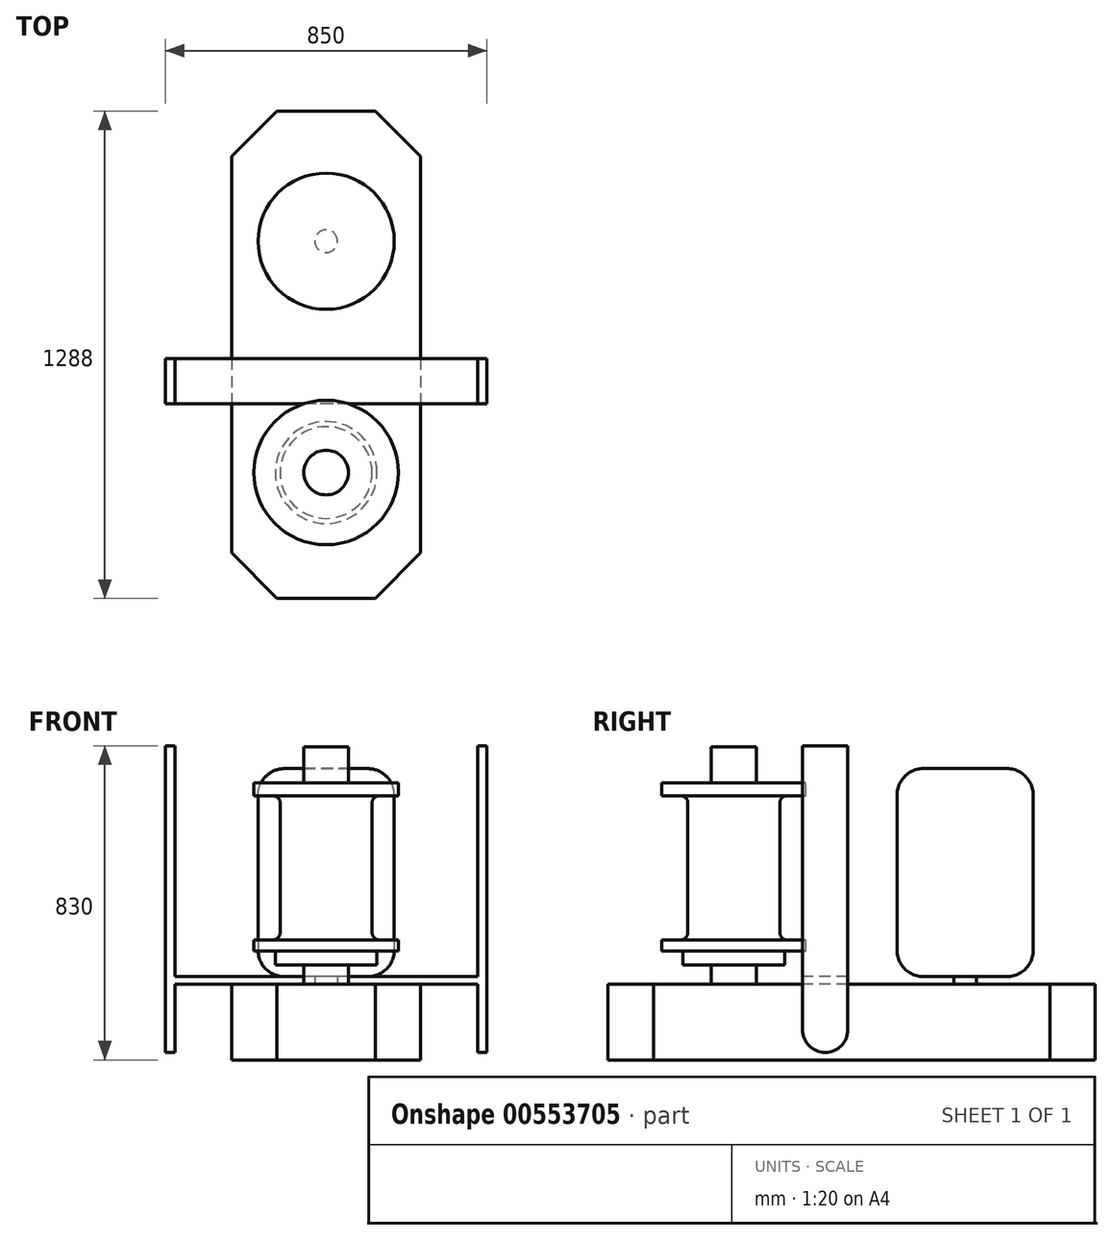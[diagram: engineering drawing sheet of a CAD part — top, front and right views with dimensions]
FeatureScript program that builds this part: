
annotation { "Feature Type Name" : "Feature", "Feature Type Description" : "" }
export const myFeature = defineFeature(function(context is Context, id is Id, definition is map)
    precondition{}
    {
        {
            var Q0;
            Q0=qCreatedBy(makeId("Top.planeOp"),FACE);
            var sketch = newSketch(context, id + "F0", { "sketchPlane" : qUnion([Q0])});
            skLineSegment(sketch, "E0.bottom", {"start": v(-130, 644) * mm, "end": v(130, 644) * mm});
            skLineSegment(sketch, "E0.top", {"start": v(-130, -644) * mm, "end": v(130, -644) * mm});
            skLineSegment(sketch, "E0.left", {"start": v(-250, 524) * mm, "end": v(-250, -524) * mm});
            skLineSegment(sketch, "E0.right", {"start": v(250, 524) * mm, "end": v(250, -524) * mm});
            skLineSegment(sketch, "E1", {"start": v(-130, 644) * mm, "end": v(-250, 524) * mm});
            skLineSegment(sketch, "E2", {"start": v(130, 644) * mm, "end": v(250, 524) * mm});
            skPoint(sketch, "E3.orphan", {"position": v(-250, 644) * mm});
            skPoint(sketch, "E4.orphan", {"position": v(250, 644) * mm});
            skLineSegment(sketch, "E5", {"start": v(-250, -524) * mm, "end": v(-130, -644) * mm});
            skPoint(sketch, "E6.orphan", {"position": v(-250, -644) * mm});
            skLineSegment(sketch, "E7", {"start": v(130, -644) * mm, "end": v(250, -524) * mm});
            skPoint(sketch, "E8.orphan", {"position": v(250, -644) * mm});
            skSolve(sketch);
        }
        {
            var Q0;
            Q0 = qSketchRegion(id + "F0", true);
            extrude(context, id + "F1", {"entities" : qUnion([Q0]), "depth" : 200 * mm, "offsetDistance" : 25 * mm});
        }
        {
            var Q0;
            Q0=makeQuery(id+"F1.opExtrude","CAP_FACE",FACE,{"disambiguationData":[OSD([sQuery(id+"F0.wireOp",EDGE,"E0.bottom"),sQuery(id+"F0.wireOp",EDGE,"E0.top"),sQuery(id+"F0.wireOp",EDGE,"E0.left"),sQuery(id+"F0.wireOp",EDGE,"E0.right"),sQuery(id+"F0.wireOp",EDGE,"E1"),sQuery(id+"F0.wireOp",EDGE,"E2"),sQuery(id+"F0.wireOp",EDGE,"E5"),sQuery(id+"F0.wireOp",EDGE,"E7")])],"isStart":false});
            var sketch = newSketch(context, id + "F2", { "sketchPlane" : qUnion([Q0])});
            skCircle(sketch, "E9", {"center": v(0, 300) * mm, "radius": 30 * mm});
            skSolve(sketch);
        }
        {
            var Q0;
            Q0=makeQuery(id+"F2.imprint","IMPRINT",FACE,{"disambiguationData":[TD([[makeQuery(id+"F2.imprint","IMPRINT",EDGE,{"derivedFrom":sQuery(id+"F2.wireOp",EDGE,"E9")}),1.0]])]});
            var Q1;
            Q1=sQuery(id+"F2.wireOp",EDGE,"E9");
            extrude(context, id + "F3", {"entities" : qUnion([Q0]), "surfaceEntities" : qUnion([Q1]), "depth" : 20 * mm, "offsetDistance" : 25 * mm});
        }
        {
            var Q0;
            Q0=makeQuery(id+"F3.opExtrude","CAP_FACE",FACE,{"disambiguationData":[OSD([sQuery(id+"F2.wireOp",EDGE,"E9")])],"isStart":false});
            var sketch = newSketch(context, id + "F4", { "sketchPlane" : qUnion([Q0])});
            skCircle(sketch, "E10", {"center": v(0, 300) * mm, "radius": 180 * mm});
            skSolve(sketch);
        }
        {
            var Q0;
            Q0=makeQuery(id+"F4.imprint","IMPRINT",FACE,{"disambiguationData":[TD([[makeQuery(id+"F4.imprint","IMPRINT",EDGE,{"derivedFrom":sQuery(id+"F4.wireOp",EDGE,"E10")}),1.0]])]});
            var Q1;
            Q1=makeQuery(id+"F4.imprint","IMPRINT",FACE,{"disambiguationData":[TD([[makeQuery(id+"F4.imprint","IMPRINT",EDGE,{"derivedFrom":makeQuery(id+"F3.opExtrude","CAP_EDGE",EDGE,{"disambiguationData":[OSD([sQuery(id+"F2.wireOp",EDGE,"E9")])],"isStart":false})}),1.0]])]});
            extrude(context, id + "F5", {"entities" : qUnion([Q0, Q1]), "operationType" : NewBodyOperationType.ADD, "depth" : 550 * mm, "offsetDistance" : 25 * mm});
        }
        {
            var Q0;
            Q0=makeQuery(id+"F5.opExtrude","CAP_EDGE",EDGE,{"disambiguationData":[OSD([sQuery(id+"F4.wireOp",EDGE,"E10")])],"isStart":false});
            var Q1;
            Q1=makeQuery(id+"F5.opExtrude","CAP_EDGE",EDGE,{"disambiguationData":[OSD([sQuery(id+"F4.wireOp",EDGE,"E10")])],"isStart":true});
            fillet(context, id + "F6", {"entities" : qUnion([Q0, Q1]), "radius" : 70 * mm, "tangentPropagation" : true, "allowEdgeOverflow" : false});
        }
        {
            var Q0;
            Q0=qCreatedBy(makeId("Right.planeOp"),FACE);
            var sketch = newSketch(context, id + "F7", { "sketchPlane" : qUnion([Q0])});
            skLineSegment(sketch, "E11", {"start": v(-311.44, 828) * mm, "end": v(-311.44, 180.1) * mm});
            skLineSegment(sketch, "E12", {"start": v(-311.44, 828) * mm, "end": v(-370.59, 828) * mm});
            skLineSegment(sketch, "E13", {"start": v(-370.59, 828) * mm, "end": v(-370.59, 732.1) * mm});
            skLineSegment(sketch, "E14", {"start": v(-370.59, 732.1) * mm, "end": v(-454.79, 732.1) * mm});
            skLineSegment(sketch, "E15", {"start": v(-454.79, 732.1) * mm, "end": v(-502.39, 732.1) * mm});
            skLineSegment(sketch, "E16", {"start": v(-502.39, 732.1) * mm, "end": v(-502.39, 698.5) * mm});
            skLineSegment(sketch, "E17", {"start": v(-502.39, 698.5) * mm, "end": v(-452.84, 698.5) * mm});
            skLineSegment(sketch, "E18", {"start": v(-432.84, 678.5) * mm, "end": v(-432.84, 337.2) * mm});
            skLineSegment(sketch, "E19", {"start": v(-452.84, 317.2) * mm, "end": v(-502.39, 317.2) * mm});
            skLineSegment(sketch, "E20", {"start": v(-502.39, 317.2) * mm, "end": v(-502.39, 287.86) * mm});
            skLineSegment(sketch, "E21", {"start": v(-502.39, 287.86) * mm, "end": v(-445.97, 287.86) * mm});
            skLineSegment(sketch, "E22", {"start": v(-445.97, 287.86) * mm, "end": v(-445.97, 250.88) * mm});
            skLineSegment(sketch, "E23", {"start": v(-445.97, 250.88) * mm, "end": v(-370.59, 250.88) * mm});
            skLineSegment(sketch, "E24", {"start": v(-370.59, 250.88) * mm, "end": v(-370.59, 175.63) * mm});
            skLineSegment(sketch, "E25", {"start": v(-370.59, 175.63) * mm, "end": v(-311.44, 180.1) * mm});
            skPoint(sketch, "E26.visualSharp", {"position": v(-432.84, 317.2) * mm});
            skArc(sketch, "E26.filletArc", {"start": v(-452.84, 317.2) * mm, "mid": v(-438.7, 323.05) * mm, "end": v(-432.84, 337.2) * mm});
            skPoint(sketch, "E27.visualSharp", {"position": v(-432.84, 698.5) * mm});
            skArc(sketch, "E27.filletArc", {"start": v(-432.84, 678.5) * mm, "mid": v(-438.7, 692.65) * mm, "end": v(-452.84, 698.5) * mm});
            skSolve(sketch);
        }
        {
            var Q0;
            Q0=makeQuery(id+"F7.imprint","IMPRINT",FACE,{"disambiguationData":[TD([[makeQuery(id+"F7.imprint","IMPRINT",EDGE,{"derivedFrom":sQuery(id+"F7.wireOp",EDGE,"E11")}),-1.0]])]});
            var Q1;
            Q1=sQuery(id+"F7.wireOp",EDGE,"E11");
            revolve(context, id + "F8", {"operationType" : NewBodyOperationType.ADD, "entities" : qUnion([Q0]), "axis" : qUnion([Q1]), "revolveType" : RevolveType.FULL});
        }
        {
            var Q0;
            Q0=makeQuery(id+"F1.opExtrude","CAP_FACE",FACE,{"disambiguationData":[OSD([sQuery(id+"F0.wireOp",EDGE,"E0.bottom"),sQuery(id+"F0.wireOp",EDGE,"E0.top"),sQuery(id+"F0.wireOp",EDGE,"E0.left"),sQuery(id+"F0.wireOp",EDGE,"E0.right"),sQuery(id+"F0.wireOp",EDGE,"E1"),sQuery(id+"F0.wireOp",EDGE,"E2"),sQuery(id+"F0.wireOp",EDGE,"E5"),sQuery(id+"F0.wireOp",EDGE,"E7")])],"isStart":false});
            var sketch = newSketch(context, id + "F9", { "sketchPlane" : qUnion([Q0])});
            skLineSegment(sketch, "E28.bottom", {"start": v(400, -10) * mm, "end": v(-400, -10) * mm});
            skLineSegment(sketch, "E28.top", {"start": v(400, -130) * mm, "end": v(-400, -130) * mm});
            skLineSegment(sketch, "E28.left", {"start": v(400, -10) * mm, "end": v(400, -130) * mm});
            skLineSegment(sketch, "E28.right", {"start": v(-400, -10) * mm, "end": v(-400, -130) * mm});
            skSolve(sketch);
        }
        {
            var Q0;
            {var subQ0=sQuery(id+"F9.wireOp",EDGE,"E28.left");Q0=makeQuery(id+"F9.imprint","IMPRINT",FACE,{"disambiguationData":[TD([[makeQuery(id+"F9.imprint","IMPRINT",EDGE,{"derivedFrom":subQ0}),-1.0]])]});}
            var Q1;
            {var subQ0=sQuery(id+"F9.wireOp",EDGE,"E28.bottom");var subQ1=makeQuery(id+"F1.opExtrude","CAP_EDGE",EDGE,{"disambiguationData":[OSD([sQuery(id+"F0.wireOp",EDGE,"E0.right")])],"isStart":false});var subQ2=makeQuery(id+"F9.imprint","INTERSECT",VERTEX,{"derivedFrom":[subQ1,subQ0]});Q1=makeQuery(id+"F9.imprint","IMPRINT",FACE,{"disambiguationData":[TD([[makeQuery(id+"F9.imprint","IMPRINT",EDGE,{"disambiguationData":[TD([[subQ2,-1.0]])],"derivedFrom":subQ0}),1.0]])]});}
            var Q2;
            {var subQ0=sQuery(id+"F9.wireOp",EDGE,"E28.right");Q2=makeQuery(id+"F9.imprint","IMPRINT",FACE,{"disambiguationData":[TD([[makeQuery(id+"F9.imprint","IMPRINT",EDGE,{"derivedFrom":subQ0}),1.0]])]});}
            extrude(context, id + "F10", {"entities" : qUnion([Q0, Q1, Q2]), "operationType" : NewBodyOperationType.ADD, "depth" : 20 * mm, "offsetDistance" : 25 * mm});
        }
        {
            var Q0;
            Q0=makeQuery(id+"F10.opExtrude","SWEPT_FACE",FACE,{"disambiguationData":[OSD([sQuery(id+"F9.wireOp",EDGE,"E28.left")])]});
            var sketch = newSketch(context, id + "F11", { "sketchPlane" : qUnion([Q0])});
            skLineSegment(sketch, "E29.top", {"start": v(-70, 20) * mm, "end": v(-70, 20) * mm});
            skLineSegment(sketch, "E29.left", {"start": v(-10, 200) * mm, "end": v(-10, 80) * mm});
            skLineSegment(sketch, "E29.right", {"start": v(-130, 200) * mm, "end": v(-130, 80) * mm});
            skLineSegment(sketch, "E30.top", {"start": v(-10, 830) * mm, "end": v(-130, 830) * mm});
            skLineSegment(sketch, "E30.left", {"start": v(-10, 200) * mm, "end": v(-10, 830) * mm});
            skLineSegment(sketch, "E30.right", {"start": v(-130, 200) * mm, "end": v(-130, 830) * mm});
            skPoint(sketch, "E31.visualSharp", {"position": v(-10, 20) * mm});
            skArc(sketch, "E31.filletArc", {"start": v(-70, 20) * mm, "mid": v(-27.57, 37.57) * mm, "end": v(-10, 80) * mm});
            skPoint(sketch, "E32.visualSharp", {"position": v(-130, 20) * mm});
            skArc(sketch, "E32.filletArc", {"start": v(-130, 80) * mm, "mid": v(-112.43, 37.57) * mm, "end": v(-70, 20) * mm});
            skSolve(sketch);
        }
        {
            var Q0;
            Q0=makeQuery(id+"F11.imprint","IMPRINT",FACE,{"disambiguationData":[TD([[makeQuery(id+"F11.imprint","IMPRINT",EDGE,{"derivedFrom":sQuery(id+"F11.wireOp",EDGE,"E29.left")}),-1.0]])]});
            var Q1;
            {var subQ0=sQuery(id+"F11.wireOp",EDGE,"E30.top");Q1=makeQuery(id+"F11.imprint","IMPRINT",FACE,{"disambiguationData":[TD([[makeQuery(id+"F11.imprint","IMPRINT",EDGE,{"derivedFrom":subQ0}),1.0]])]});}
            var Q2;
            {var subQ1=sQuery(id+"F9.wireOp",EDGE,"E28.left");var subQ2=makeQuery(id+"F10.opExtrude","CAP_EDGE",EDGE,{"disambiguationData":[OSD([subQ1])],"isStart":true});Q2=makeQuery(id+"F11.imprint","IMPRINT",FACE,{"disambiguationData":[TD([[makeQuery(id+"F11.imprint","IMPRINT",EDGE,{"derivedFrom":subQ2}),-1.0]])]});}
            extrude(context, id + "F12", {"entities" : qUnion([Q0, Q1, Q2]), "operationType" : NewBodyOperationType.ADD, "depth" : 25 * mm, "offsetDistance" : 25 * mm});
        }
        {
            var Q0;
            Q0=makeQuery(id+"F10.opExtrude","SWEPT_FACE",FACE,{"disambiguationData":[OSD([sQuery(id+"F9.wireOp",EDGE,"E28.right")])]});
            var sketch = newSketch(context, id + "F13", { "sketchPlane" : qUnion([Q0])});
            skLineSegment(sketch, "E33.bottom", {"start": v(10, 830) * mm, "end": v(130, 830) * mm});
            skLineSegment(sketch, "E33.top", {"start": v(70, 20) * mm, "end": v(70, 20) * mm});
            skLineSegment(sketch, "E33.left", {"start": v(10, 830) * mm, "end": v(10, 80) * mm});
            skLineSegment(sketch, "E33.right", {"start": v(130, 830) * mm, "end": v(130, 80) * mm});
            skPoint(sketch, "E34.visualSharp", {"position": v(130, 20) * mm});
            skArc(sketch, "E34.filletArc", {"start": v(70, 20) * mm, "mid": v(112.43, 37.57) * mm, "end": v(130, 80) * mm});
            skPoint(sketch, "E35.visualSharp", {"position": v(10, 20) * mm});
            skArc(sketch, "E35.filletArc", {"start": v(10, 80) * mm, "mid": v(27.57, 37.57) * mm, "end": v(70, 20) * mm});
            skSolve(sketch);
        }
        {
            var Q0;
            {var subQ0=sQuery(id+"F13.wireOp",EDGE,"E33.bottom");Q0=makeQuery(id+"F13.imprint","IMPRINT",FACE,{"disambiguationData":[TD([[makeQuery(id+"F13.imprint","IMPRINT",EDGE,{"derivedFrom":subQ0}),-1.0]])]});}
            var Q1;
            {var subQ0=sQuery(id+"F13.wireOp",EDGE,"E34.filletArc");Q1=makeQuery(id+"F13.imprint","IMPRINT",FACE,{"disambiguationData":[TD([[makeQuery(id+"F13.imprint","IMPRINT",EDGE,{"derivedFrom":subQ0}),1.0]])]});}
            var Q2;
            {var subQ1=sQuery(id+"F9.wireOp",EDGE,"E28.right");var subQ2=makeQuery(id+"F10.opExtrude","CAP_EDGE",EDGE,{"disambiguationData":[OSD([subQ1])],"isStart":true});Q2=makeQuery(id+"F13.imprint","IMPRINT",FACE,{"disambiguationData":[TD([[makeQuery(id+"F13.imprint","IMPRINT",EDGE,{"derivedFrom":subQ2}),1.0]])]});}
            extrude(context, id + "F14", {"entities" : qUnion([Q0, Q1, Q2]), "operationType" : NewBodyOperationType.ADD, "depth" : 25 * mm, "offsetDistance" : 25 * mm});
        }
    });
